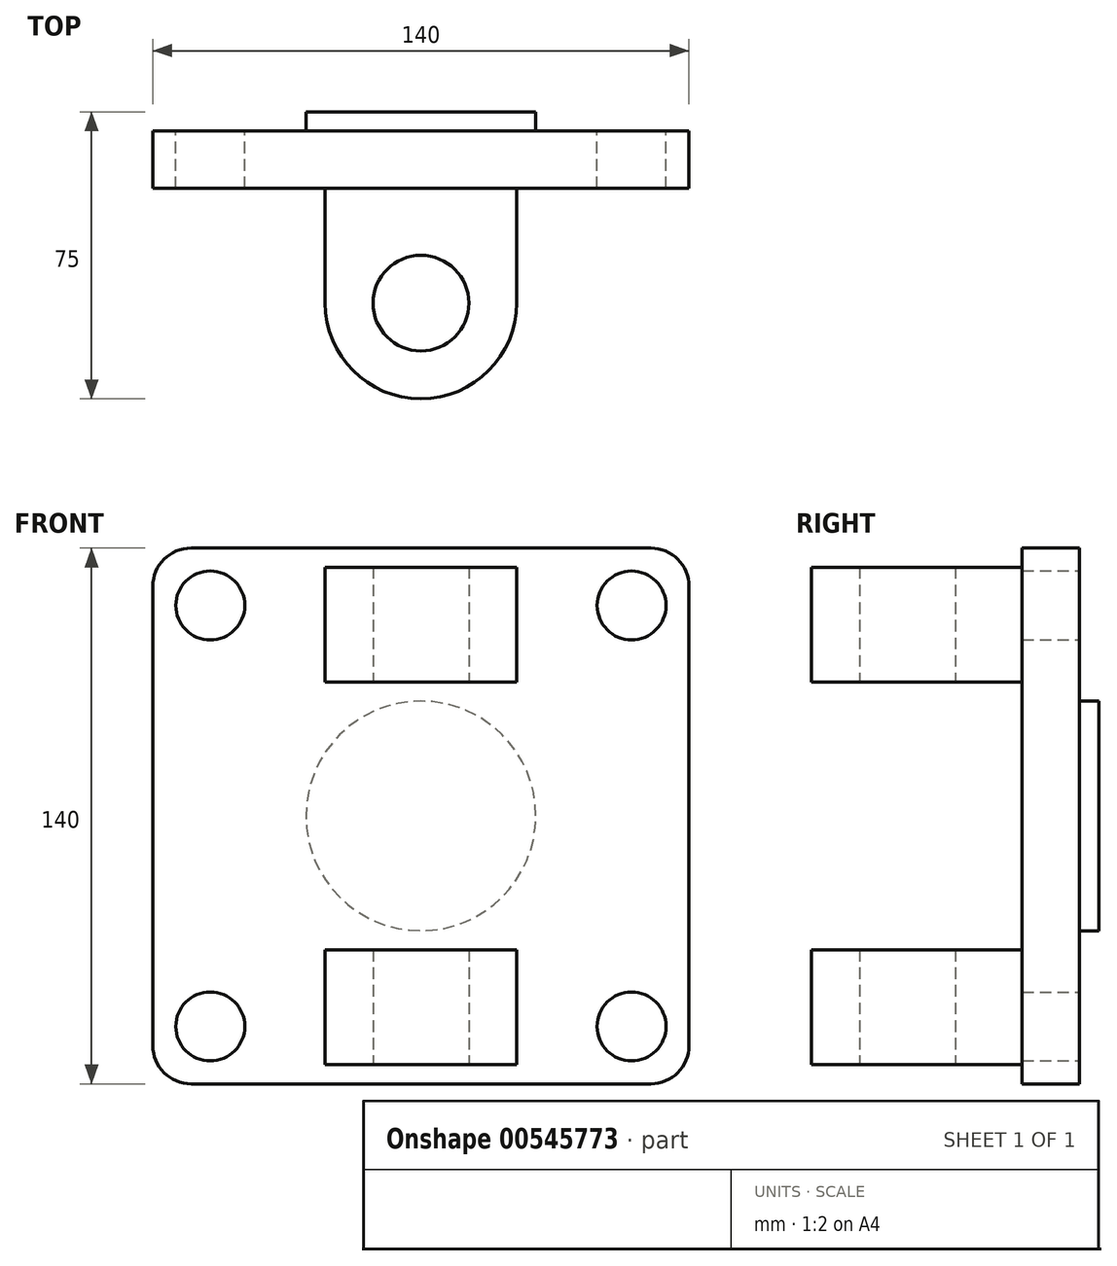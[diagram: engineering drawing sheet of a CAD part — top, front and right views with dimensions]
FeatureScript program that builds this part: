
annotation { "Feature Type Name" : "Feature", "Feature Type Description" : "" }
export const myFeature = defineFeature(function(context is Context, id is Id, definition is map)
    precondition{}
    {
        {
            var Q0;
            Q0=qCreatedBy(makeId("Front.planeOp"),FACE);
            var sketch = newSketch(context, id + "F0", { "sketchPlane" : qUnion([Q0])});
            skLineSegment(sketch, "E0.bottom", {"start": v(60, -70) * mm, "end": v(-60, -70) * mm});
            skLineSegment(sketch, "E0.top", {"start": v(60, 70) * mm, "end": v(-60, 70) * mm});
            skLineSegment(sketch, "E0.left", {"start": v(70, -60) * mm, "end": v(70, 60) * mm});
            skLineSegment(sketch, "E0.right", {"start": v(-70, -60) * mm, "end": v(-70, 60) * mm});
            skPoint(sketch, "E0.middle", {"position": v(0, 0) * mm});
            skPoint(sketch, "E1.visualSharp", {"position": v(-70, 70) * mm});
            skArc(sketch, "E1.filletArc", {"start": v(-60, 70) * mm, "mid": v(-67.07, 67.07) * mm, "end": v(-70, 60) * mm});
            skPoint(sketch, "E2.visualSharp", {"position": v(70, 70) * mm});
            skArc(sketch, "E2.filletArc", {"start": v(70, 60) * mm, "mid": v(67.07, 67.07) * mm, "end": v(60, 70) * mm});
            skPoint(sketch, "E3.visualSharp", {"position": v(70, -70) * mm});
            skArc(sketch, "E3.filletArc", {"start": v(60, -70) * mm, "mid": v(67.07, -67.07) * mm, "end": v(70, -60) * mm});
            skPoint(sketch, "E4.visualSharp", {"position": v(-70, -70) * mm});
            skArc(sketch, "E4.filletArc", {"start": v(-70, -60) * mm, "mid": v(-67.07, -67.07) * mm, "end": v(-60, -70) * mm});
            skLineSegment(sketch, "E5", {"start": v(0, 70) * mm, "end": v(0, -70) * mm, "construction": true});
            skLineSegment(sketch, "E6.0", {"start": v(-55, 47.5) * mm, "end": v(-55, -47.5) * mm, "construction": true});
            skLineSegment(sketch, "E7.0", {"start": v(55, 47.5) * mm, "end": v(55, -47.5) * mm, "construction": true});
            skLineSegment(sketch, "E8", {"start": v(-70, 0) * mm, "end": v(70, 0) * mm, "construction": true});
            skLineSegment(sketch, "E9.0", {"start": v(-47.5, -55) * mm, "end": v(47.5, -55) * mm, "construction": true});
            skLineSegment(sketch, "E10.0", {"start": v(-47.5, 55) * mm, "end": v(47.5, 55) * mm, "construction": true});
            skCircle(sketch, "E11", {"center": v(-55, 55) * mm, "radius": 9 * mm});
            skCircle(sketch, "E12", {"center": v(55, 55) * mm, "radius": 9 * mm});
            skCircle(sketch, "E13", {"center": v(-55, -55) * mm, "radius": 9 * mm});
            skCircle(sketch, "E14", {"center": v(55, -55) * mm, "radius": 9 * mm});
            skSolve(sketch);
        }
        {
            var Q0;
            Q0=makeQuery(id+"F0.imprint","IMPRINT",FACE,{"disambiguationData":[TD([[makeQuery(id+"F0.imprint","IMPRINT",EDGE,{"derivedFrom":sQuery(id+"F0.wireOp",EDGE,"E0.bottom")}),-1.0]])]});
            extrude(context, id + "F1", {"entities" : qUnion([Q0]), "endBound" : BoundingType.SYMMETRIC, "depth" : 20 * mm, "offsetDistance" : 25 * mm});
        }
        {
            var Q0;
            Q0=makeQuery(id+"F1.opExtrude","CAP_FACE",FACE,{"disambiguationData":[OSD([sQuery(id+"F0.wireOp",EDGE,"E0.bottom"),sQuery(id+"F0.wireOp",EDGE,"E0.top"),sQuery(id+"F0.wireOp",EDGE,"E0.left"),sQuery(id+"F0.wireOp",EDGE,"E0.right"),sQuery(id+"F0.wireOp",EDGE,"E1.filletArc"),sQuery(id+"F0.wireOp",EDGE,"E2.filletArc"),sQuery(id+"F0.wireOp",EDGE,"E3.filletArc"),sQuery(id+"F0.wireOp",EDGE,"E4.filletArc"),sQuery(id+"F0.wireOp",EDGE,"E11"),sQuery(id+"F0.wireOp",EDGE,"E12"),sQuery(id+"F0.wireOp",EDGE,"E13"),sQuery(id+"F0.wireOp",EDGE,"E14")])],"isStart":false});
            var sketch = newSketch(context, id + "F2", { "sketchPlane" : qUnion([Q0])});
            skCircle(sketch, "E15", {"center": v(0, 0) * mm, "radius": 30 * mm});
            skSolve(sketch);
        }
        {
            var Q0;
            Q0=qCreatedBy(makeId("Top.planeOp"),FACE);
            var sketch = newSketch(context, id + "F3", { "sketchPlane" : qUnion([Q0])});
            skLineSegment(sketch, "E16", {"start": v(62.06, -40) * mm, "end": v(-61.89, -40) * mm, "construction": true});
            skLineSegment(sketch, "E17", {"start": v(0, 0) * mm, "end": v(0, -54.12) * mm, "construction": true});
            skArc(sketch, "E18", {"start": v(-25, -40) * mm, "mid": v(0, -65) * mm, "end": v(25, -40) * mm});
            skCircle(sketch, "E19", {"center": v(0, -40) * mm, "radius": 12.5 * mm});
            skLineSegment(sketch, "E20.0", {"start": v(30, -10) * mm, "end": v(-30, -10) * mm});
            skLineSegment(sketch, "E21", {"start": v(25, -40) * mm, "end": v(25, -10) * mm});
            skLineSegment(sketch, "E22", {"start": v(-25, -40) * mm, "end": v(-25, -10) * mm});
            skSolve(sketch);
        }
        {
            var Q0;
            Q0=makeQuery(id+"F3.imprint","IMPRINT",FACE,{"disambiguationData":[TD([[makeQuery(id+"F3.imprint","IMPRINT",EDGE,{"derivedFrom":sQuery(id+"F3.wireOp",EDGE,"E18")}),1.0]])]});
            extrude(context, id + "F4", {"entities" : qUnion([Q0]), "operationType" : NewBodyOperationType.ADD, "endBound" : BoundingType.SYMMETRIC, "depth" : 130 * mm, "offsetDistance" : 25 * mm});
        }
        {
            var Q0;
            Q0 = qSketchRegion(id + "F3", true);
            extrude(context, id + "F5", {"entities" : qUnion([Q0]), "endBound" : BoundingType.SYMMETRIC, "depth" : 70 * mm, "offsetDistance" : 25 * mm});
        }
        {
            var Q0;
            Q0=makeQuery(id+"F5.opExtrude","SWEPT_BODY",BODY,{"disambiguationData":[OSD([sQuery(id+"F3.wireOp",EDGE,"E18"),sQuery(id+"F3.wireOp",EDGE,"E19"),sQuery(id+"F3.wireOp",EDGE,"E20.0"),sQuery(id+"F3.wireOp",EDGE,"E21"),sQuery(id+"F3.wireOp",EDGE,"E22")])]});
            var Q1;
            Q1=makeQuery(id+"F1.opExtrude","SWEPT_BODY",BODY,{"disambiguationData":[OSD([sQuery(id+"F0.wireOp",EDGE,"E0.bottom"),sQuery(id+"F0.wireOp",EDGE,"E0.top"),sQuery(id+"F0.wireOp",EDGE,"E0.left"),sQuery(id+"F0.wireOp",EDGE,"E0.right"),sQuery(id+"F0.wireOp",EDGE,"E1.filletArc"),sQuery(id+"F0.wireOp",EDGE,"E2.filletArc"),sQuery(id+"F0.wireOp",EDGE,"E3.filletArc"),sQuery(id+"F0.wireOp",EDGE,"E4.filletArc"),sQuery(id+"F0.wireOp",EDGE,"E11"),sQuery(id+"F0.wireOp",EDGE,"E12"),sQuery(id+"F0.wireOp",EDGE,"E13"),sQuery(id+"F0.wireOp",EDGE,"E14")])]});
            booleanBodies(context, id + "F6", {"operationType" : BooleanOperationType.SUBTRACTION, "tools" : qUnion([Q0]), "targets" : qUnion([Q1])});
        }
        {
            var Q0;
            Q0=makeQuery(id+"F1.opExtrude","CAP_FACE",FACE,{"disambiguationData":[OSD([sQuery(id+"F0.wireOp",EDGE,"E0.bottom"),sQuery(id+"F0.wireOp",EDGE,"E0.top"),sQuery(id+"F0.wireOp",EDGE,"E0.left"),sQuery(id+"F0.wireOp",EDGE,"E0.right"),sQuery(id+"F0.wireOp",EDGE,"E1.filletArc"),sQuery(id+"F0.wireOp",EDGE,"E2.filletArc"),sQuery(id+"F0.wireOp",EDGE,"E3.filletArc"),sQuery(id+"F0.wireOp",EDGE,"E4.filletArc"),sQuery(id+"F0.wireOp",EDGE,"E11"),sQuery(id+"F0.wireOp",EDGE,"E12"),sQuery(id+"F0.wireOp",EDGE,"E13"),sQuery(id+"F0.wireOp",EDGE,"E14")])],"isStart":true});
            var sketch = newSketch(context, id + "F7", { "sketchPlane" : qUnion([Q0])});
            skCircle(sketch, "E23.0", {"center": v(0, 0) * mm, "radius": 30 * mm});
            skSolve(sketch);
        }
        {
            var Q0;
            Q0=makeQuery(id+"F7.imprint","IMPRINT",FACE,{"disambiguationData":[TD([[makeQuery(id+"F7.imprint","IMPRINT",EDGE,{"derivedFrom":sQuery(id+"F7.wireOp",EDGE,"E23.0")}),-1.0]])]});
            extrude(context, id + "F8", {"entities" : qUnion([Q0]), "operationType" : NewBodyOperationType.REMOVE, "oppositeDirection" : true, "depth" : 5 * mm, "offsetDistance" : 25 * mm});
        }
    });
